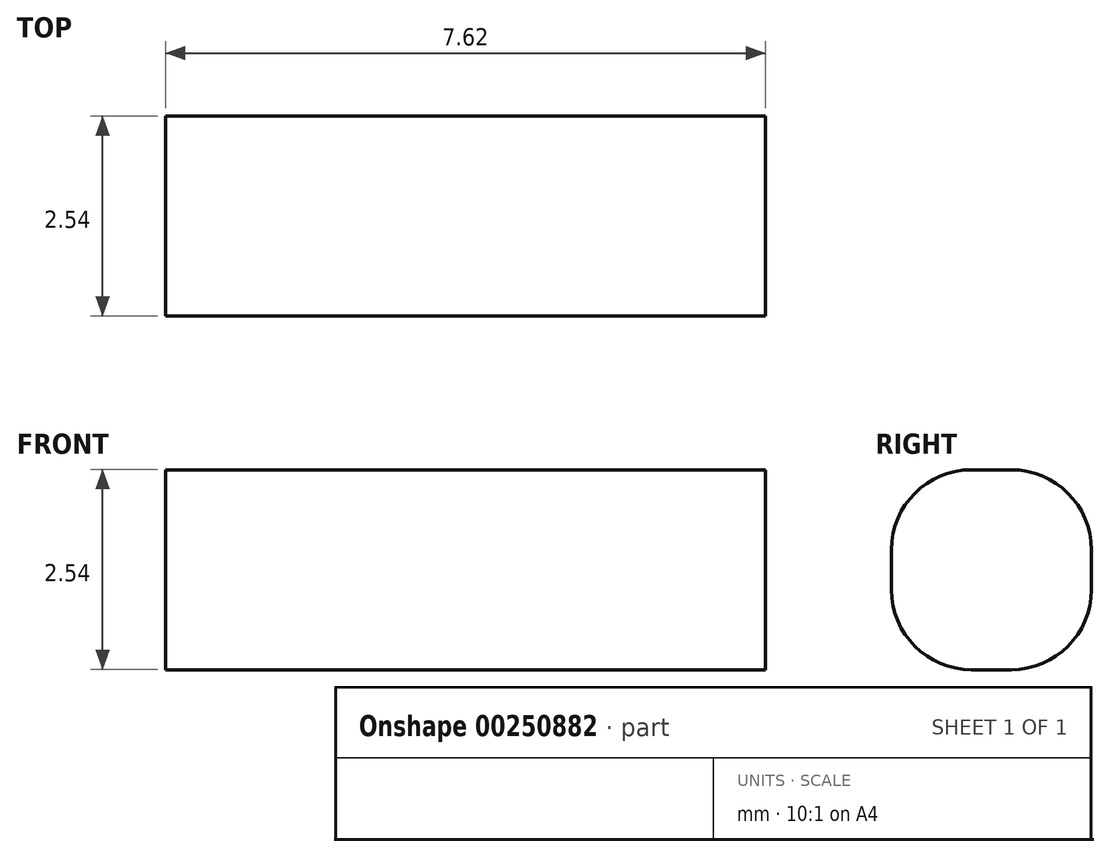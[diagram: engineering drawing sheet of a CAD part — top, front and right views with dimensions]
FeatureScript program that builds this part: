
annotation { "Feature Type Name" : "Feature", "Feature Type Description" : "" }
export const myFeature = defineFeature(function(context is Context, id is Id, definition is map)
    precondition{}
    {
        {
            var Q0;
            Q0=qCreatedBy(makeId("Front.planeOp"),FACE);
            var sketch = newSketch(context, id + "F0", { "sketchPlane" : qUnion([Q0])});
            skLineSegment(sketch, "E0.bottom", {"start": v(-2.57, -0.41) * mm, "end": v(5.05, -0.41) * mm});
            skLineSegment(sketch, "E0.top", {"start": v(-2.57, -2.95) * mm, "end": v(5.05, -2.95) * mm});
            skLineSegment(sketch, "E0.left", {"start": v(-2.57, -0.41) * mm, "end": v(-2.57, -2.95) * mm});
            skLineSegment(sketch, "E0.right", {"start": v(5.05, -0.41) * mm, "end": v(5.05, -2.95) * mm});
            skSolve(sketch);
        }
        {
            var Q0;
            Q0=makeQuery(id+"F0.imprint","IMPRINT",FACE,{"disambiguationData":[TD([[makeQuery(id+"F0.imprint","IMPRINT",EDGE,{"derivedFrom":sQuery(id+"F0.wireOp",EDGE,"E0.bottom")}),-1.0]])]});
            extrude(context, id + "F1", {"entities" : qUnion([Q0]), "depth" : 2.54 * mm});
        }
        {
            var Q0;
            Q0=makeQuery(id+"F1.opExtrude","CAP_EDGE",EDGE,{"disambiguationData":[OSD([sQuery(id+"F0.wireOp",EDGE,"E0.top")])],"isStart":true});
            fillet(context, id + "F2", {"entities" : qUnion([Q0]), "radius" : 1.02 * mm, "tangentPropagation" : true, "allowEdgeOverflow" : false});
        }
        {
            var Q0;
            Q0=makeQuery(id+"F1.opExtrude","CAP_EDGE",EDGE,{"disambiguationData":[OSD([sQuery(id+"F0.wireOp",EDGE,"E0.top")])],"isStart":false});
            fillet(context, id + "F3", {"entities" : qUnion([Q0]), "radius" : 1.02 * mm, "tangentPropagation" : true, "allowEdgeOverflow" : false});
        }
        {
            var Q0;
            Q0=makeQuery(id+"F1.opExtrude","CAP_EDGE",EDGE,{"disambiguationData":[OSD([sQuery(id+"F0.wireOp",EDGE,"E0.bottom")])],"isStart":false});
            fillet(context, id + "F4", {"entities" : qUnion([Q0]), "radius" : 1.02 * mm, "tangentPropagation" : true, "allowEdgeOverflow" : false});
        }
        {
            var Q0;
            Q0=makeQuery(id+"F1.opExtrude","CAP_EDGE",EDGE,{"disambiguationData":[OSD([sQuery(id+"F0.wireOp",EDGE,"E0.bottom")])],"isStart":true});
            fillet(context, id + "F5", {"entities" : qUnion([Q0]), "radius" : 1.02 * mm, "tangentPropagation" : true, "allowEdgeOverflow" : false});
        }
    });
